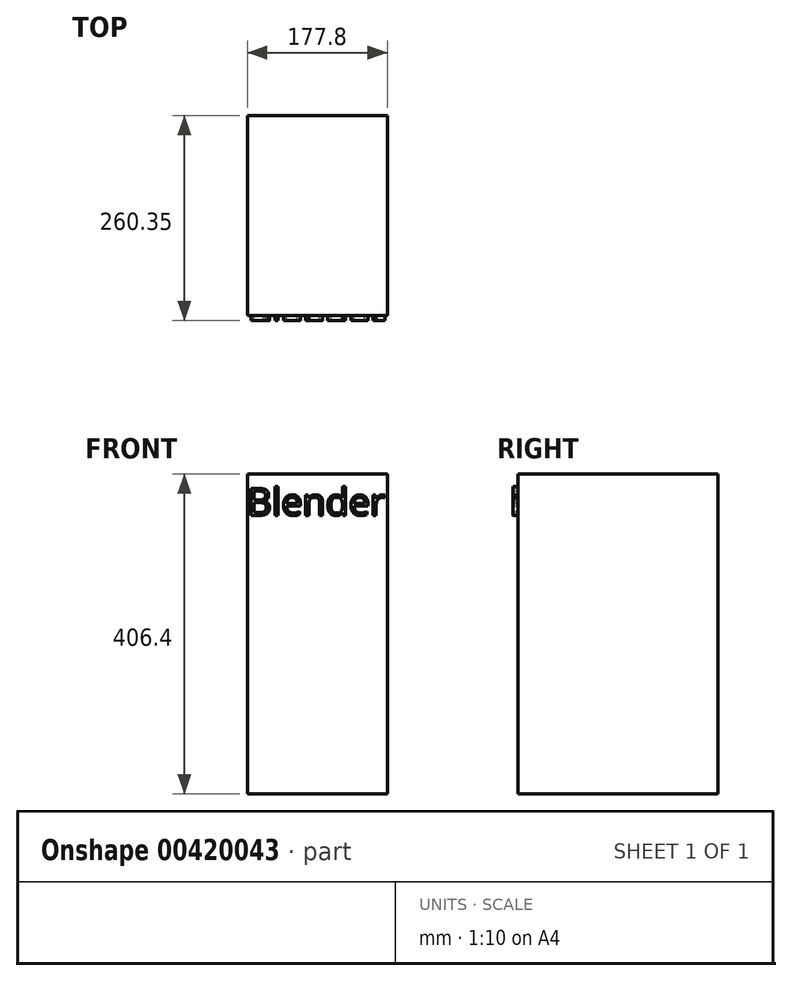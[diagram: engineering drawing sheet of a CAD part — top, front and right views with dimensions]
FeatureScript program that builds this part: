
annotation { "Feature Type Name" : "Feature", "Feature Type Description" : "" }
export const myFeature = defineFeature(function(context is Context, id is Id, definition is map)
    precondition{}
    {
        {
            var Q0;
            Q0=qCreatedBy(makeId("Front.planeOp"),FACE);
            var sketch = newSketch(context, id + "F0", { "sketchPlane" : qUnion([Q0])});
            skLineSegment(sketch, "E0.bottom", {"start": v(0, 0) * mm, "end": v(177.8, 0) * mm});
            skLineSegment(sketch, "E0.top", {"start": v(0, 406.4) * mm, "end": v(177.8, 406.4) * mm});
            skLineSegment(sketch, "E0.left", {"start": v(0, 0) * mm, "end": v(0, 406.4) * mm});
            skLineSegment(sketch, "E0.right", {"start": v(177.8, 0) * mm, "end": v(177.8, 406.4) * mm});
            skSolve(sketch);
        }
        {
            var Q0;
            Q0 = qSketchRegion(id + "F0", true);
            extrude(context, id + "F1", {"entities" : qUnion([Q0]), "depth" : 254 * mm});
        }
        {
            var Q0;
            Q0=makeQuery(id+"F1.opExtrude","CAP_FACE",FACE,{"disambiguationData":[OSD([sQuery(id+"F0.wireOp",EDGE,"E0.bottom"),sQuery(id+"F0.wireOp",EDGE,"E0.top"),sQuery(id+"F0.wireOp",EDGE,"E0.left"),sQuery(id+"F0.wireOp",EDGE,"E0.right")])],"isStart":false});
            var sketch = newSketch(context, id + "F2", { "sketchPlane" : qUnion([Q0])});
            skText(sketch, "E1", { "text": "Blender", "fontName": "OpenSans-Regular.ttf"});
            const initialGuessF2  = {"E1": [0, 0.35396, 1, 0, 0.03452]};
            skSetInitialGuess(sketch, initialGuessF2);
            skSolve(sketch);
        }
        {
            var Q0;
            Q0 = qSketchRegion(id + "F2", true);
            extrude(context, id + "F3", {"entities" : qUnion([Q0]), "operationType" : NewBodyOperationType.ADD, "depth" : 6.35 * mm});
        }
    });
